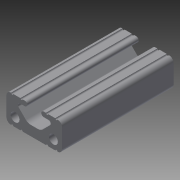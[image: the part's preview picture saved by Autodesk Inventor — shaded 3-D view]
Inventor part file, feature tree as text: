
AUTODESK INVENTOR PART (.ipt)
format: ipt  version: 2014 SP2 (Build 180246200, 246)  size: 135,168 bytes
history: native  units: in
note: dims shown in document units (in); Inventor stores cm internally (conversion verified against a paired STEP export)
features: extrude x1, sketch x1
ambient origin geometry x8: Origin, YZ Plane, XZ Plane, XY Plane, X Axis, Y Axis, Z Axis, Center Point
bodies: Solid1 (feature_tree)
feature tree (2):
  extrude  "Extrusion1"  [1 undecoded]
  sketch  "Sketch_1"  dims[d0=2.0in d1=0.0in]
note: 1 required parameter value undecoded (feature->parameter linkage not recoverable at this tier; creation-order binding heuristic only, values carry confidence <= 0.55)
